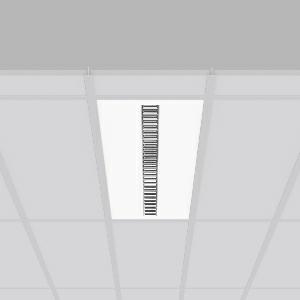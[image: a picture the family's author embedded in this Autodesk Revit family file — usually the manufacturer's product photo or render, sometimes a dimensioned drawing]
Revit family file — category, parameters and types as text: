
# Revit family: sonis_901681_002_1_76_7d14
name_source: partatom
category: Lighting Fixtures
units: mm (PartAtom-declared; Revit-internal decimal feet)

## family parameters
Cut with Voids When Loaded = No
Host = Face
Light Source = No
Part Type = Normal
Room Calculation Point = No
Round Connector Dimension = Use Diameter
Shared = No

## types (1)
- SONIS (1 x LED Modul 840, 3450 lm, 4000)
    Apparent Load = 26 VA
    CIE Flux Codes = 83 100 100 100 100
    Color Rendering = 80
    Color Temperature = 4000
    Default Elevation = 1800 mm
    Description = Series: SONIS
High-efficiency lay-in luminaire for ceiling systems with visible mounting rails. Housing: metal, powder-coated. Alea optical system: Reflector structure (ABS, Aluminium-coated, highly polished) with integrated diffuser made of non-yellowing plastic (PMMA) opal for glare-free light at the workstation. Narrow beam, brilliant luminous effect. Suitable for Recessed ceiling mounting. Driver integrated. Perfect for office areas (RUG < 19) and environments with computer screens in accordance with EN 12464-1. 
Colour: white
Length: 1247 mm
Width: 310 mm
Cut-out length: 1225 mm
Cut-out width: 285 mm
Recess height: 27 mm
Lamp: LED
Socket: without socket
Colour temperature: 4000K
Colour rendering index (CRI): 80
System power: 26 W
Rated luminous flux: 3450 lm
Luminous efficiency: 133 lm/W
Control gear: Converter, dimmable, DALI
Protection class: I
Type of protection: IP 20
    Height = 0 mm  [stored 0 ft]
    Lamp = 1 x LED Modul 840
    Lamp Light Flux = 3450 lm
    Lamp count = 1
    Length = 1247 mm
    Lifetime = 50000 h
    Luminous efficacy = 133 lm/W
    Manufacturer = RZB
    ModVariant = No
    Model = 901681.002.1.76
    Mounting Place = Ceiling
    Mounting Type = Recessed
    Number of Poles = 1
    OnlyDefault = Yes
    Power Factor = 1
    Product Name = SONIS
    Product group = Recessed modular luminaires
    ProductGroupID = 406
    Protection Class = Protection class I
    Protection Degree = IP 20
    RLX_Detail_Level = 1
    RLX_Emergency_Light_Flux = 0 lm
    RLX_Emergency_Type = 0
    RLX_Emergency_Type_DB = No
    RlxData = <blob elided: 33429 chars, md5=d2663dbf>
    Socket = socket
    Standby Power = 0 W
    System Light Flux = 3450 lm
    System Power = 26 W
    Type Comments = Product without accessories
    Type Image = 901623.002.jpg
    URL = http://relux.com
    VarID = ---
    Voltage = 0 V
    Weight = 0.00 kg
    Width = 310 mm

note: [stored X ft] marks values corroborated as IEEE doubles in the binary element streams (Revit-internal decimal feet)

## geometry (parser evidence)
native form markers: Blend x4, Sweep x12
no freeform markers — native parametric forms only
